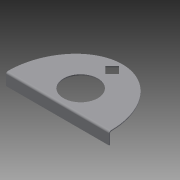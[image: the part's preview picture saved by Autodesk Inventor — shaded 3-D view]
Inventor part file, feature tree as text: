
AUTODESK INVENTOR PART (.ipt)
format: ipt  version: 2015 SP1 (Build 190203100, 203)  size: 116,224 bytes
history: native  units: mm
features: extrude x2, fillet x2, sketch x1
ambient origin geometry x8: Origin, YZ Plane, XZ Plane, XY Plane, X Axis, Y Axis, Z Axis, Center Point
bodies: Body1 (feature_tree)
feature tree (5):
  extrude  "Extrusion3"  Depth=2.0mm
  extrude  "Extrusion4"  Depth=2.0mm
  fillet  "Fillet1"  Radius=45.0mm
  fillet  "Fillet2"  Radius=95.0mm
  sketch  "Sketch2"  dims[d0=105.0mm d1=20.0mm d2=20.0mm d26=45.0mm d29=95.0mm d32=70.0mm d33=130.0mm d34=2.0mm d35=0.0mm d36=2.0mm d37=25.0mm d38=0.0mm d39=4.0mm d40=2.0mm]
